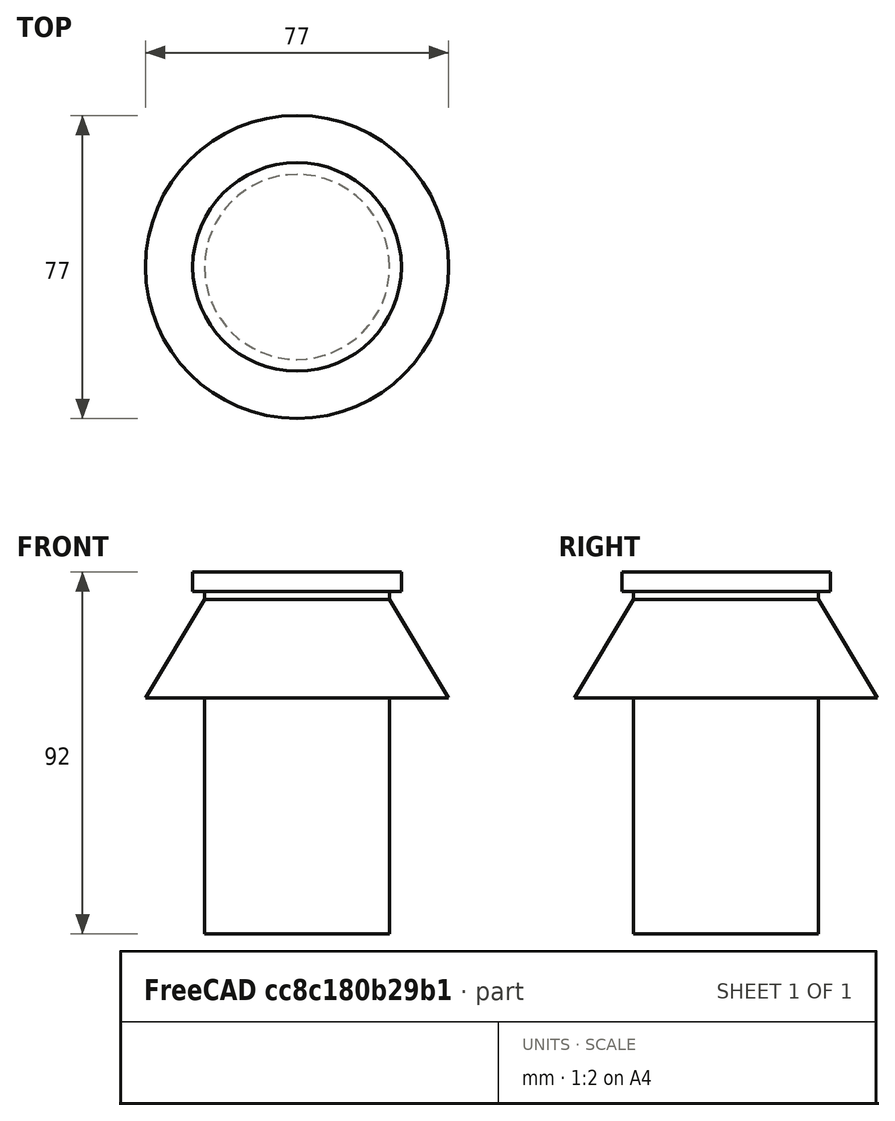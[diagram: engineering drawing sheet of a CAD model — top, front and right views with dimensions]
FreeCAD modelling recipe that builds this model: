
FCSTD DOCUMENT  (FreeCAD 1.1R38926 (Git))
Label: Штамп
License: All rights reserved
LicenseURL: https://en.wikipedia.org/wiki/All_rights_reserved
objects: Sketcher::SketchObject×1, PartDesign::Revolution×1, PartDesign::Body×1
note: 6 computed .brp shape members not serialized (recipe doc carries the construction recipe); baked Part::Feature solids carry a one-line shape summary decoded from their .brp

FEATURE [Sketcher::SketchObject] Sketch
  ArcFitTolerance = 1e-06
  AttachmentSupport = -> [XZ_Plane]
  FullyConstrained = true
  MakeInternals = false
  MapMode = 5
  Placement = pos=(0,0,0) rot=(1,0,0;1.5708rad)
  sketch-geometry (10):
    g0: LineSegment StartX=0 StartY=0 StartZ=0 EndX=-23.5 EndY=0 EndZ=0
    g1: LineSegment StartX=-23.5 StartY=0 StartZ=0 EndX=-23.5 EndY=60 EndZ=0
    g2: LineSegment StartX=-23.5 StartY=60 StartZ=0 EndX=-38.5 EndY=60 EndZ=0
    g3: LineSegment StartX=-38.5 StartY=60 StartZ=0 EndX=-23.5 EndY=85 EndZ=0
    g4: LineSegment StartX=-26.5 StartY=92 StartZ=0 EndX=0 EndY=92 EndZ=0
    g5: LineSegment StartX=0 StartY=92 StartZ=0 EndX=0 EndY=0 EndZ=0
    g6: LineSegment [constr] StartX=-23.5 StartY=60 StartZ=0 EndX=-23.5 EndY=85 EndZ=0
    g7: LineSegment StartX=-23.5 StartY=85 StartZ=0 EndX=-23.5 EndY=87 EndZ=0
    g8: LineSegment StartX=-23.5 StartY=87 StartZ=0 EndX=-26.5 EndY=87 EndZ=0
    g9: LineSegment StartX=-26.5 StartY=87 StartZ=0 EndX=-26.5 EndY=92 EndZ=0
  constraints (28):
    c: Coincident(g-1,g0)
    c: PointOnObject(g0,g-1)
    c: Coincident(g0,g1)
    c: Vertical(g1)
    c: Coincident(g1,g2)
    c: Horizontal(g2)
    c: Coincident(g2,g3)
    c: PointOnObject(g4,g-2)
    c: Coincident(g4,g5)
    c: Coincident(g5,g0)
    c: Horizontal(g4)
    c: DistanceY(g1,g1) = 60
    c: Distance(g2,g2) = 15
    c: Coincident(g6,g1)
    c: DistanceX(g0,g0) = 23.5
    c: DistanceY(g2,g4) = 32
    c: Coincident(g3,g7)
    c: Coincident(g7,g8)
    c: Horizontal(g8)
    c: Coincident(g8,g9)
    c: Vertical(g9)
    c: Coincident(g4,g9)
    c: Coincident(g6,g3)
    c: Distance(g8,g8) = 3
    c: Vertical(g7)
    c: Vertical(g6)
    c: DistanceY(g9,g9) = 5
    c: DistanceY(g3,g3) = 25
FEATURE [PartDesign::Revolution] Revolution
  Angle = 360
  Angle2 = 60
  Axis = (0,2e-16,1)
  Base = (0,0,0)
  Placement = pos=(0,0,0) rot=(1,0,0;1.5708rad)
  Profile = -> Sketch
  ReferenceAxis = -> Sketch [V_Axis]
  Refine = true
  Suppressed = false
  Type = 0
FEATURE [PartDesign::Body] Body  label="Тело"
  AllowCompound = false
  Group = -> [Sketch,Revolution]
  Origin = -> Origin
  Tip = -> Revolution
